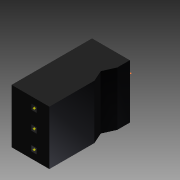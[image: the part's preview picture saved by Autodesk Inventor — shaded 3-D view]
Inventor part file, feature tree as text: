
AUTODESK INVENTOR PART (.ipt)
format: ipt  version: 2013 (Build 170138000, 138)  size: 121,856 bytes
history: native  units: in
note: dims shown in document units (in); Inventor stores cm internally (conversion verified against a paired STEP export)
features: other x12, plane x8, sketch x4, extrude x3
ambient origin geometry x8: Origin, YZ Plane, XZ Plane, XY Plane, X Axis, Y Axis, Z Axis, Center Point
bodies: Solid1 (feature_tree)
feature tree (27):
  extrude  "Extrusion1"  Depth=0.0241in
  sketch  "Sketch2"  dims[d3=1.0in d4=0.0in d5=0.125in]
  extrude  "Extrusion2"  Depth=0.125in
  other  "Work Point8"
  other  "Work Point9"
  other  "Work Point10"
  other  "Work Point11"
  other  "Work Point12"
  other  "Work Point13"
  extrude  "Extrusion3"  Depth=0.25in
  sketch  "Sketch1"  dims[d0=0.197in d1=0.0in d2=0.0241in]
  sketch  "Sketch3"  dims[d6=0.125in d7=0.25in]
  plane  "Work Plane5"
  plane  "Work Plane6"
  other  "Work Axis4"
  plane  "Work Plane7"
  plane  "Work Plane8"
  other  "Work Axis5"
  plane  "Work Plane9"
  other  "Work Axis6"
  plane  "Work Plane10"
  other  "Work Axis7"
  plane  "Work Plane11"
  other  "Work Axis8"
  plane  "Work Plane12"
  other  "Work Axis9"
  sketch  "Sketch4"  dims[d8=0.25in d9=0.125in d10=0.25in d11=0.125in d12=0.25in d13=0.25in d14=0.0in]
